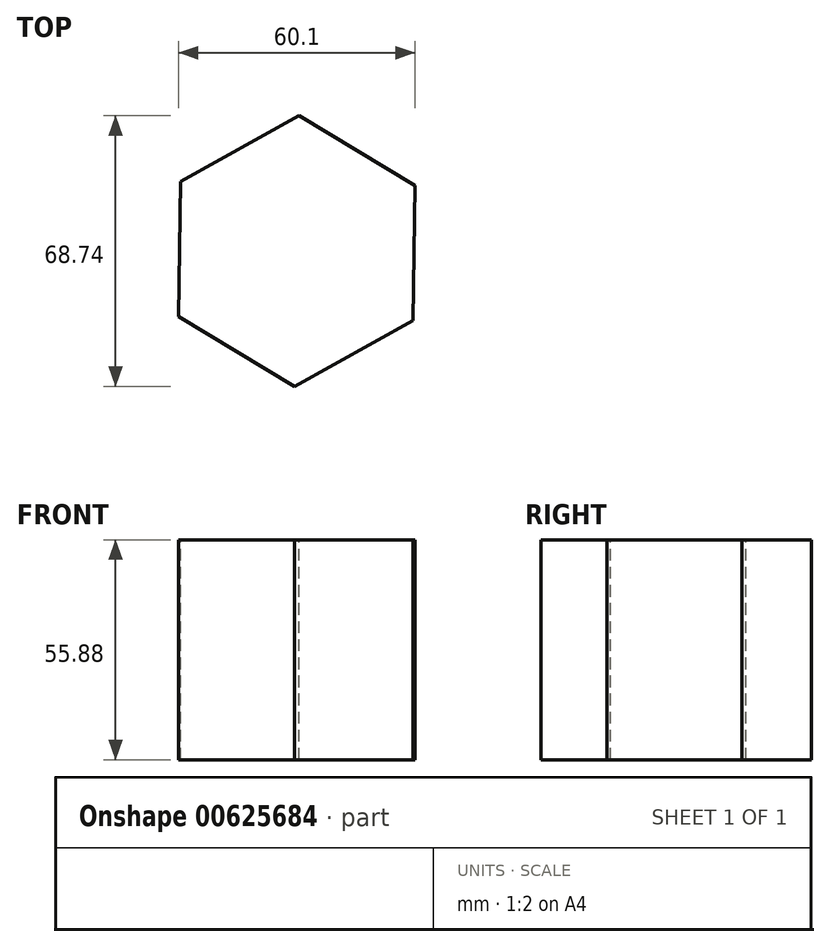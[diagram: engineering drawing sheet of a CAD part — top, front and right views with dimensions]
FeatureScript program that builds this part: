
annotation { "Feature Type Name" : "Feature", "Feature Type Description" : "" }
export const myFeature = defineFeature(function(context is Context, id is Id, definition is map)
    precondition{}
    {
        {
            var Q0;
            Q0=qCreatedBy(makeId("Top.planeOp"),FACE);
            var sketch = newSketch(context, id + "F0", { "sketchPlane" : qUnion([Q0])});
            skCircle(sketch, "E0.cCircle", {"center": v(0, 0) * mm, "radius": 29.77 * mm, "construction": true});
            skLineSegment(sketch, "E0.0", {"start": v(-29.48, 17.67) * mm, "end": v(0.56, 34.37) * mm});
            skLineSegment(sketch, "E0.1", {"start": v(0.56, 34.37) * mm, "end": v(30.05, 16.7) * mm});
            skLineSegment(sketch, "E0.2", {"start": v(30.05, 16.7) * mm, "end": v(29.48, -17.67) * mm});
            skLineSegment(sketch, "E0.3", {"start": v(29.48, -17.67) * mm, "end": v(-0.56, -34.37) * mm});
            skLineSegment(sketch, "E0.4", {"start": v(-0.56, -34.37) * mm, "end": v(-30.05, -16.7) * mm});
            skLineSegment(sketch, "E0.5", {"start": v(-30.05, -16.7) * mm, "end": v(-29.48, 17.67) * mm});
            skPoint(sketch, "E0.0.midPoint", {"position": v(-14.46, 26.02) * mm});
            skSolve(sketch);
        }
        {
            var Q0;
            Q0=makeQuery(id+"F0.imprint","IMPRINT",FACE,{"disambiguationData":[TD([[makeQuery(id+"F0.imprint","IMPRINT",EDGE,{"derivedFrom":sQuery(id+"F0.wireOp",EDGE,"E0.0")}),-1.0]])]});
            extrude(context, id + "F1", {"entities" : qUnion([Q0]), "oppositeDirection" : true, "depth" : 55.88 * mm, "offsetDistance" : 25.4 * mm});
        }
    });
